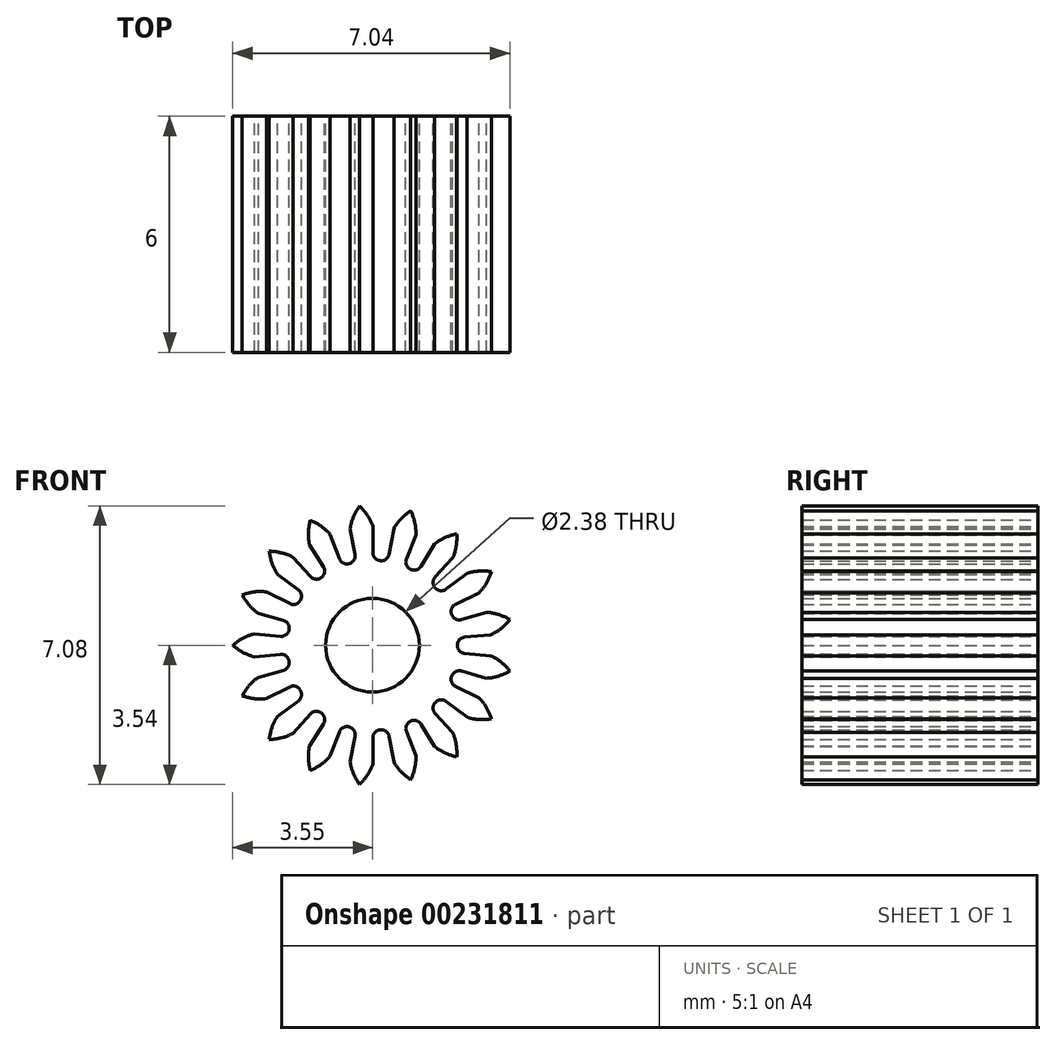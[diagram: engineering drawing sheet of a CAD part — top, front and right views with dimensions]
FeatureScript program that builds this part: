
annotation { "Feature Type Name" : "Feature", "Feature Type Description" : "" }
export const myFeature = defineFeature(function(context is Context, id is Id, definition is map)
    precondition{}
    {
        {
            assignVariable(context, id + "F0", {"name" : "Teeth", "anyValue" : 17});
        }
        {
            var Q0;
            Q0=qCreatedBy(makeId("Front.planeOp"),FACE);
            var sketch = newSketch(context, id + "F1", { "sketchPlane" : qUnion([Q0])});
            skCircle(sketch, "E0", {"center": v(0, 0) * mm, "radius": 2.91 * mm, "construction": true});
            skLineSegment(sketch, "E1", {"start": v(0, 0) * mm, "end": v(-0.22, 2.9) * mm, "construction": true});
            skLineSegment(sketch, "E2", {"start": v(0, 0) * mm, "end": v(-0.48, 2.88) * mm, "construction": true});
            skLineSegment(sketch, "E3", {"start": v(0, 0) * mm, "end": v(-0.73, 2.82) * mm, "construction": true});
            skLineSegment(sketch, "E4", {"start": v(-0.73, 2.82) * mm, "end": v(0.01, 3.01) * mm, "construction": true});
            skLineSegment(sketch, "E5", {"start": v(0, 0) * mm, "end": v(-0.97, 2.75) * mm, "construction": true});
            skLineSegment(sketch, "E6", {"start": v(-0.97, 2.75) * mm, "end": v(-0.01, 3.09) * mm, "construction": true});
            skLineSegment(sketch, "E7", {"start": v(-0.73, 2.82) * mm, "end": v(-0.48, 2.88) * mm, "construction": true});
            skLineSegment(sketch, "E8", {"start": v(-0.97, 2.75) * mm, "end": v(-0.73, 2.82) * mm, "construction": true});
            skLineSegment(sketch, "E9", {"start": v(-0.73, 2.82) * mm, "end": v(-0.22, 2.9) * mm, "construction": true});
            skLineSegment(sketch, "E10", {"start": v(-0.97, 2.75) * mm, "end": v(-0.22, 2.9) * mm, "construction": true});
            skLineSegment(sketch, "E11", {"start": v(0, 0) * mm, "end": v(-1.65, 2.4) * mm, "construction": true});
            skLineSegment(sketch, "E12", {"start": v(-1.65, 2.4) * mm, "end": v(-0.2, 3.4) * mm, "construction": true});
            skLineSegment(sketch, "E13", {"start": v(0, 0) * mm, "end": v(-1.43, 2.54) * mm, "construction": true});
            skLineSegment(sketch, "E14", {"start": v(-1.43, 2.54) * mm, "end": v(-0.12, 3.28) * mm, "construction": true});
            skLineSegment(sketch, "E15", {"start": v(0, 0) * mm, "end": v(-1.2, 2.65) * mm, "construction": true});
            skLineSegment(sketch, "E16", {"start": v(-1.2, 2.65) * mm, "end": v(-0.05, 3.18) * mm, "construction": true});
            skLineSegment(sketch, "E17", {"start": v(-1.2, 2.65) * mm, "end": v(-0.97, 2.75) * mm, "construction": true});
            skLineSegment(sketch, "E18", {"start": v(-1.2, 2.65) * mm, "end": v(-1.43, 2.54) * mm, "construction": true});
            skLineSegment(sketch, "E19", {"start": v(-1.43, 2.54) * mm, "end": v(-1.65, 2.4) * mm, "construction": true});
            skLineSegment(sketch, "E20", {"start": v(-1.2, 2.65) * mm, "end": v(-0.22, 2.9) * mm, "construction": true});
            skLineSegment(sketch, "E21", {"start": v(-1.43, 2.54) * mm, "end": v(-0.22, 2.9) * mm, "construction": true});
            skLineSegment(sketch, "E22", {"start": v(-1.65, 2.4) * mm, "end": v(-0.22, 2.9) * mm, "construction": true});
            skLineSegment(sketch, "E23", {"start": v(0, 0) * mm, "end": v(-2.04, 2.08) * mm, "construction": true});
            skLineSegment(sketch, "E24", {"start": v(-2.04, 2.08) * mm, "end": v(-0.45, 3.64) * mm, "construction": true});
            skLineSegment(sketch, "E25", {"start": v(0, 0) * mm, "end": v(-2.21, 1.9) * mm, "construction": true});
            skLineSegment(sketch, "E26", {"start": v(-2.21, 1.9) * mm, "end": v(-0.61, 3.77) * mm, "construction": true});
            skLineSegment(sketch, "E27", {"start": v(0, 0) * mm, "end": v(-2.37, 1.7) * mm, "construction": true});
            skLineSegment(sketch, "E28", {"start": v(0, 0) * mm, "end": v(-1.85, 2.25) * mm, "construction": true});
            skLineSegment(sketch, "E29", {"start": v(-1.85, 2.25) * mm, "end": v(-0.3, 3.52) * mm, "construction": true});
            skLineSegment(sketch, "E30", {"start": v(-1.65, 2.4) * mm, "end": v(-1.85, 2.25) * mm, "construction": true});
            skLineSegment(sketch, "E31", {"start": v(-1.85, 2.25) * mm, "end": v(-2.04, 2.08) * mm, "construction": true});
            skLineSegment(sketch, "E32", {"start": v(-2.04, 2.08) * mm, "end": v(-2.21, 1.9) * mm, "construction": true});
            skLineSegment(sketch, "E33", {"start": v(-2.21, 1.9) * mm, "end": v(-2.37, 1.7) * mm, "construction": true});
            skLineSegment(sketch, "E34", {"start": v(-0.22, 2.9) * mm, "end": v(-1.85, 2.25) * mm, "construction": true});
            skLineSegment(sketch, "E35", {"start": v(-0.22, 2.9) * mm, "end": v(-2.04, 2.08) * mm, "construction": true});
            skLineSegment(sketch, "E36", {"start": v(-0.22, 2.9) * mm, "end": v(-2.21, 1.9) * mm, "construction": true});
            skLineSegment(sketch, "E37", {"start": v(-0.22, 2.9) * mm, "end": v(-2.37, 1.7) * mm, "construction": true});
            skCircle(sketch, "E38", {"center": v(0, 0) * mm, "radius": 3.05 * mm, "construction": true});
            skCircle(sketch, "E39", {"center": v(0, 0) * mm, "radius": 3.82 * mm});
            skPoint(sketch, "E40", {"position": v(0, 3.05) * mm});
            skLineSegment(sketch, "E41", {"start": v(0, 0) * mm, "end": v(-0.8, 8.56) * mm, "construction": true});
            skPoint(sketch, "E42.MirrorP", {"position": v(-0.56, 3) * mm});
            skLineSegment(sketch, "E43", {"start": v(-0.56, 3) * mm, "end": v(0, 0) * mm, "construction": true});
            skLineSegment(sketch, "E44", {"start": v(0, 0) * mm, "end": v(0, 3.05) * mm, "construction": true});
            skLineSegment(sketch, "E45", {"start": v(-0.48, 2.88) * mm, "end": v(-0.22, 2.9) * mm, "construction": true});
            skLineSegment(sketch, "E46", {"start": v(0.01, 3.01) * mm, "end": v(-0.01, 3.09) * mm, "construction": true});
            skLineSegment(sketch, "E47", {"start": v(0, 0) * mm, "end": v(0, 10.19) * mm, "construction": true});
            skCircle(sketch, "E48", {"center": v(0, 0) * mm, "radius": 2.16 * mm});
            skSolve(sketch);
        }
        {
            var Q0;
            Q0=qCreatedBy(makeId("Front.planeOp"),FACE);
            var sketch = newSketch(context, id + "F2", { "sketchPlane" : qUnion([Q0])});
            skCircle(sketch, "E49.0", {"center": v(0, 0) * mm, "radius": 3.05 * mm, "construction": true});
            skPoint(sketch, "E50.0", {"position": v(-0.61, 3.77) * mm});
            skPoint(sketch, "E50.1", {"position": v(-0.45, 3.64) * mm});
            skPoint(sketch, "E50.2", {"position": v(-0.3, 3.52) * mm});
            skPoint(sketch, "E50.3", {"position": v(-0.2, 3.4) * mm});
            skPoint(sketch, "E50.4", {"position": v(-0.12, 3.28) * mm});
            skPoint(sketch, "E50.6", {"position": v(-0.01, 3.09) * mm});
            skPoint(sketch, "E50.7", {"position": v(0.01, 3.01) * mm});
            skPoint(sketch, "E50.8", {"position": v(-0.05, 3.18) * mm});
            skLineSegment(sketch, "E51.0", {"start": v(0, 0) * mm, "end": v(-0.8, 8.56) * mm, "construction": true});
            skFitSpline(sketch, "E52", {"points": [v(-0.61, 3.77) * mm, v(-0.45, 3.64) * mm, v(-0.3, 3.52) * mm, v(-0.2, 3.4) * mm, v(-0.12, 3.28) * mm, v(-0.05, 3.18) * mm, v(-0.01, 3.09) * mm, v(0.01, 3.01) * mm], "startDerivative": vector(2.84, -2.14) * mm, "endDerivative": vector(0.72, -2.06) * mm});
            skFitSpline(sketch, "E53.MirrorCS", {"points": [v(-0.1, 3.82) * mm, v(-0.23, 3.66) * mm, v(-0.34, 3.52) * mm, v(-0.43, 3.38) * mm, v(-0.49, 3.25) * mm, v(-0.53, 3.13) * mm, v(-0.55, 3.04) * mm, v(-0.57, 2.96) * mm], "startDerivative": vector(-2.4, -2.63) * mm, "endDerivative": vector(-0.33, -2.16) * mm});
            skCircle(sketch, "E54", {"center": v(0, 0) * mm, "radius": 1.2 * mm});
            skCircle(sketch, "E55.0", {"center": v(0, 0) * mm, "radius": 2.16 * mm});
            skArc(sketch, "E56", {"start": v(-0.61, 3.77) * mm, "mid": v(0.35, -3.8) * mm, "end": v(-0.1, 3.82) * mm});
            skLineSegment(sketch, "E57", {"start": v(-0.57, 2.96) * mm, "end": v(0, 0) * mm});
            skLineSegment(sketch, "E58", {"start": v(0, 0) * mm, "end": v(0.01, 3.01) * mm});
            skSolve(sketch);
        }
        {
            var Q0;
            {var subQ1=sQuery(id+"F2.wireOp",EDGE,"E52");var subQ9=sQuery(id+"F2.wireOp",EDGE,"rA0usyOi-Jm6w-jZNR-JSDv-ujEcH4bsm2Ol");var subQ11=makeQuery(id+"F2.imprint","INTERSECT",VERTEX,{"derivedFrom":[subQ1,subQ9]});Q0=makeQuery(id+"F2.imprint","IMPRINT",FACE,{"disambiguationData":[TD([[makeQuery(id+"F2.imprint","IMPRINT",EDGE,{"disambiguationData":[TD([[subQ11,1.0]])],"derivedFrom":subQ1}),-1.0]])]});}
            var Q1;
            {var subQ0=sQuery(id+"F2.wireOp",EDGE,"QqPcIgQ4-TZE6-73E5-WQaq-ugCT5JtziKyn");var subQ1=sQuery(id+"F2.wireOp",EDGE,"90be38e0-c88f-493d-85a8-1201295b9109.0");var subQ2=makeQuery(id+"F2.imprint","INTERSECT",VERTEX,{"derivedFrom":[subQ1,subQ0]});Q1=makeQuery(id+"F2.imprint","IMPRINT",FACE,{"disambiguationData":[TD([[makeQuery(id+"F2.imprint","IMPRINT",EDGE,{"disambiguationData":[TD([[subQ2,1.0]])],"derivedFrom":subQ1}),1.0]])]});}
            var Q2;
            {var subQ0=sQuery(id+"F2.wireOp",EDGE,"QqPcIgQ4-TZE6-73E5-WQaq-ugCT5JtziKyn");var subQ1=sQuery(id+"F2.wireOp",EDGE,"90be38e0-c88f-493d-85a8-1201295b9109.0");var subQ2=makeQuery(id+"F2.imprint","INTERSECT",VERTEX,{"derivedFrom":[subQ1,subQ0]});Q2=makeQuery(id+"F2.imprint","IMPRINT",FACE,{"disambiguationData":[TD([[makeQuery(id+"F2.imprint","IMPRINT",EDGE,{"disambiguationData":[TD([[subQ2,-1.0]])],"derivedFrom":subQ1}),1.0]])]});}
            var Q3;
            {var subQ1=sQuery(id+"F2.wireOp",EDGE,"E52");var subQ8=sQuery(id+"F2.wireOp",EDGE,"b861a5ab-cd51-40f1-92ab-cea0f5fe0d4d.1");var subQ11=makeQuery(id+"F2.imprint","INTERSECT",VERTEX,{"derivedFrom":[subQ1,subQ8]});Q3=makeQuery(id+"F2.imprint","IMPRINT",FACE,{"disambiguationData":[TD([[makeQuery(id+"F2.imprint","IMPRINT",EDGE,{"disambiguationData":[TD([[subQ11,1.0]])],"derivedFrom":subQ1}),-1.0]])]});}
            var Q4;
            {var subQ0=sQuery(id+"F2.wireOp",EDGE,"b861a5ab-cd51-40f1-92ab-cea0f5fe0d4d.0");var subQ1=sQuery(id+"F2.wireOp",EDGE,"E54");var subQ2=makeQuery(id+"F2.imprint","INTERSECT",VERTEX,{"derivedFrom":[subQ1,subQ0]});Q4=makeQuery(id+"F2.imprint","IMPRINT",FACE,{"disambiguationData":[TD([[makeQuery(id+"F2.imprint","IMPRINT",EDGE,{"disambiguationData":[TD([[subQ2,-1.0]])],"derivedFrom":subQ1}),-1.0]])]});}
            var Q5;
            {var subQ0=sQuery(id+"F2.wireOp",EDGE,"b861a5ab-cd51-40f1-92ab-cea0f5fe0d4d.0");var subQ1=sQuery(id+"F2.wireOp",EDGE,"E54");var subQ2=makeQuery(id+"F2.imprint","INTERSECT",VERTEX,{"derivedFrom":[subQ1,subQ0]});Q5=makeQuery(id+"F2.imprint","IMPRINT",FACE,{"disambiguationData":[TD([[makeQuery(id+"F2.imprint","IMPRINT",EDGE,{"disambiguationData":[TD([[subQ2,1.0]])],"derivedFrom":subQ1}),-1.0]])]});}
            extrude(context, id + "F3", {"entities" : qUnion([Q0, Q1, Q2, Q3, Q4, Q5]), "offsetDistance" : 25 * mm, "depth" : 6 * mm});
        }
        {
            var Q0;
            Q0=makeQuery(id+"F3.opExtrude","SWEPT_EDGE",EDGE,{"disambiguationData":[OSD([sQuery(id+"F2.wireOp",EDGE,"b861a5ab-cd51-40f1-92ab-cea0f5fe0d4d.1"),sQuery(id+"F2.wireOp",EDGE,"E55.0")])]});
            var Q1;
            Q1=makeQuery(id+"F3.opExtrude","SWEPT_EDGE",EDGE,{"disambiguationData":[OSD([sQuery(id+"F2.wireOp",EDGE,"b861a5ab-cd51-40f1-92ab-cea0f5fe0d4d.0"),sQuery(id+"F2.wireOp",EDGE,"E55.0")])]});
            fillet(context, id + "F4", {"entities" : qUnion([Q0, Q1]), "radius" : 0.2 * mm, "tangentPropagation" : true, "allowEdgeOverflow" : false});
        }
        {
            var Q0;
            Q0=makeQuery(id+"F4.opFillet","BLEND_FACE",FACE,{"disambiguationData":[OSD([sQuery(id+"F2.wireOp",EDGE,"E55.0"),sQuery(id+"F2.wireOp",EDGE,"E57")])]});
            var Q1;
            Q1=makeQuery(id+"F3.opExtrude","SWEPT_FACE",FACE,{"disambiguationData":[OSD([sQuery(id+"F2.wireOp",EDGE,"E57")])]});
            var Q2;
            Q2=makeQuery(id+"F3.opExtrude","SWEPT_FACE",FACE,{"disambiguationData":[OSD([sQuery(id+"F2.wireOp",EDGE,"E53.MirrorCS")])]});
            var Q3;
            Q3=makeQuery(id+"F3.opExtrude","SWEPT_FACE",FACE,{"disambiguationData":[OSD([sQuery(id+"F2.wireOp",EDGE,"E56")])]});
            var Q4;
            Q4=makeQuery(id+"F3.opExtrude","SWEPT_FACE",FACE,{"disambiguationData":[OSD([sQuery(id+"F2.wireOp",EDGE,"E52")])]});
            var Q5;
            Q5=makeQuery(id+"F3.opExtrude","SWEPT_FACE",FACE,{"disambiguationData":[OSD([sQuery(id+"F2.wireOp",EDGE,"E58")])]});
            var Q6;
            Q6=makeQuery(id+"F4.opFillet","BLEND_FACE",FACE,{"disambiguationData":[OSD([sQuery(id+"F2.wireOp",EDGE,"E55.0"),sQuery(id+"F2.wireOp",EDGE,"E58")])]});
            var Q7;
            Q7=makeQuery(id+"F3.opExtrude","SWEPT_FACE",FACE,{"disambiguationData":[OSD([sQuery(id+"F2.wireOp",EDGE,"E55.0")])]});
            circularPattern(context, id + "F5", {"faces" : qUnion([Q0, Q1, Q2, Q3, Q4, Q5, Q6]), "axis" : qUnion([Q7]), "angle" : 360 * degree, "instanceCount" : round(getVariable(context, 'Teeth')), "equalSpace" : true, "patternType" : PatternType.FACE});
        }
    });
